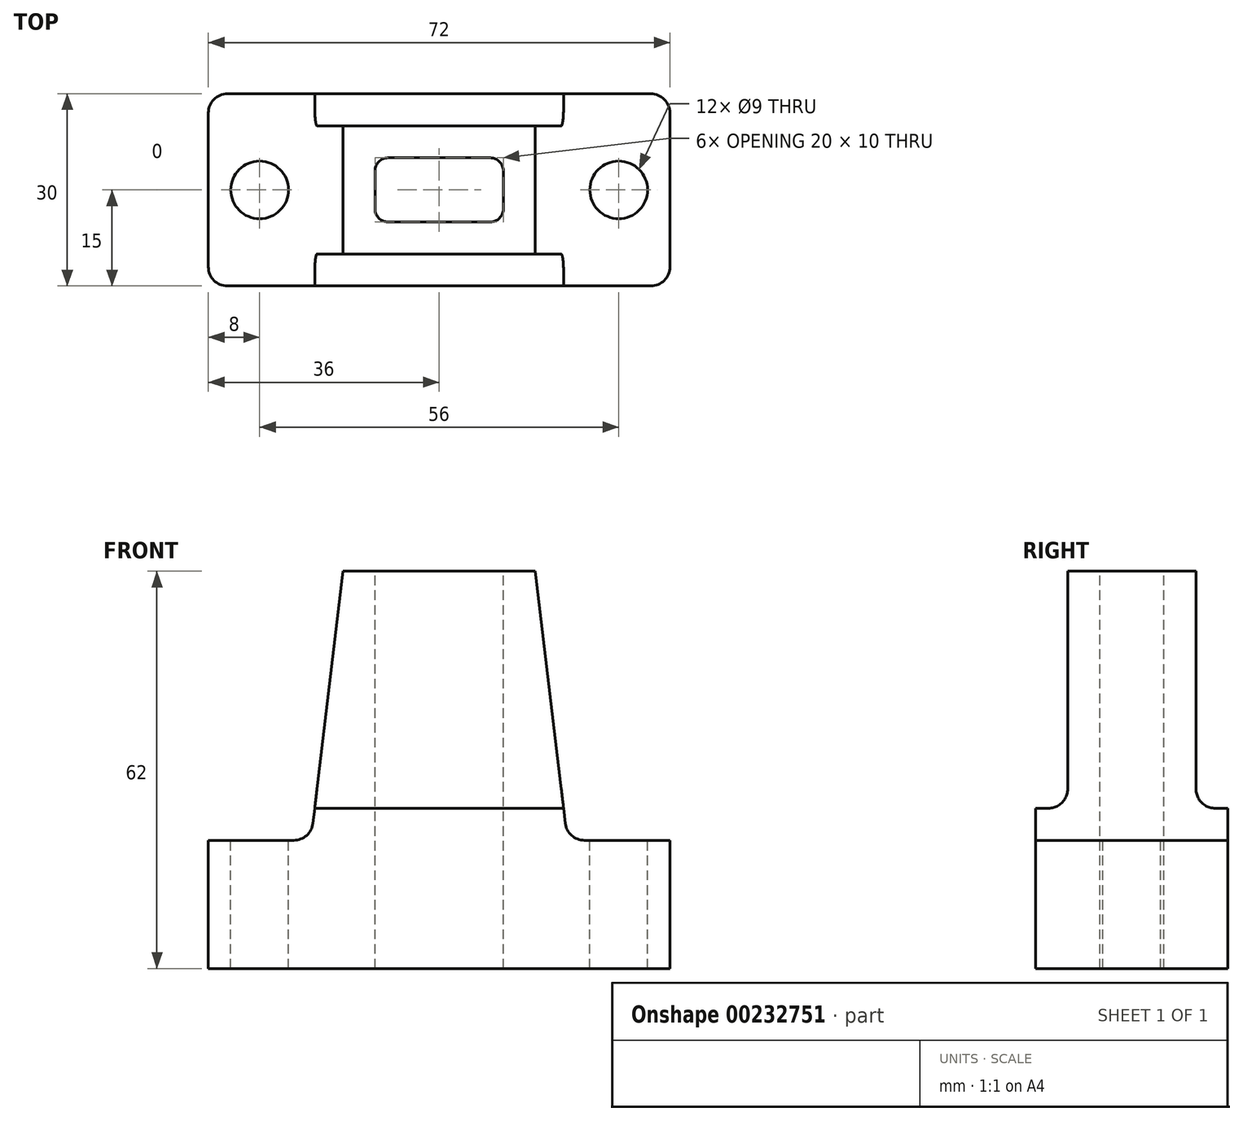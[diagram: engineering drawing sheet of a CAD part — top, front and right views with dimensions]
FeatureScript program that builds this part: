
annotation { "Feature Type Name" : "Feature", "Feature Type Description" : "" }
export const myFeature = defineFeature(function(context is Context, id is Id, definition is map)
    precondition{}
    {
        {
            var Q0;
            Q0=qCreatedBy(makeId("Top.planeOp"),FACE);
            var sketch = newSketch(context, id + "F0", { "sketchPlane" : qUnion([Q0])});
            skLineSegment(sketch, "E0.bottom", {"start": v(-36, 15) * mm, "end": v(36, 15) * mm});
            skLineSegment(sketch, "E0.top", {"start": v(-36, -15) * mm, "end": v(36, -15) * mm});
            skLineSegment(sketch, "E0.left", {"start": v(-36, 15) * mm, "end": v(-36, -15) * mm});
            skLineSegment(sketch, "E0.right", {"start": v(36, 15) * mm, "end": v(36, -15) * mm});
            skSolve(sketch);
        }
        {
            var Q0;
            Q0 = qSketchRegion(id + "F0", true);
            extrude(context, id + "F1", {"entities" : qUnion([Q0]), "depth" : 62 * mm});
        }
        {
            var Q0;
            Q0=makeQuery(id+"F1.opExtrude","SWEPT_FACE",FACE,{"disambiguationData":[OSD([sQuery(id+"F0.wireOp",EDGE,"E0.top")])]});
            var sketch = newSketch(context, id + "F2", { "sketchPlane" : qUnion([Q0])});
            skLineSegment(sketch, "E1", {"start": v(-46, 72) * mm, "end": v(-15, 72) * mm});
            skLineSegment(sketch, "E2", {"start": v(-15, 72) * mm, "end": v(-15, 62) * mm});
            skLineSegment(sketch, "E3", {"start": v(-15, 62) * mm, "end": v(-20, 20) * mm});
            skLineSegment(sketch, "E4", {"start": v(-20, 20) * mm, "end": v(-46, 20) * mm});
            skLineSegment(sketch, "E5", {"start": v(-46, 20) * mm, "end": v(-46, 72) * mm});
            skLineSegment(sketch, "E6.MirrorCS", {"start": v(15, 72) * mm, "end": v(15, 62) * mm});
            skLineSegment(sketch, "E7.MirrorCS", {"start": v(20, 20) * mm, "end": v(46, 20) * mm});
            skLineSegment(sketch, "E8.MirrorCS", {"start": v(46, 72) * mm, "end": v(15, 72) * mm});
            skLineSegment(sketch, "E9.MirrorCS", {"start": v(15, 62) * mm, "end": v(20, 20) * mm});
            skLineSegment(sketch, "E10.MirrorCS", {"start": v(46, 20) * mm, "end": v(46, 72) * mm});
            skSolve(sketch);
        }
        {
            var Q0;
            Q0 = qSketchRegion(id + "F2", true);
            extrude(context, id + "F3", {"entities" : qUnion([Q0]), "operationType" : NewBodyOperationType.REMOVE, "endBound" : BoundingType.THROUGH_ALL, "oppositeDirection" : true, "depth" : 25 * mm});
        }
        {
            var Q0;
            Q0=qCreatedBy(makeId("Right.planeOp"),FACE);
            var sketch = newSketch(context, id + "F4", { "sketchPlane" : qUnion([Q0])});
            skLineSegment(sketch, "E11.bottom", {"start": v(-25, 72) * mm, "end": v(-10, 72) * mm});
            skLineSegment(sketch, "E11.top", {"start": v(-25, 25) * mm, "end": v(-10, 25) * mm});
            skLineSegment(sketch, "E11.left", {"start": v(-25, 72) * mm, "end": v(-25, 25) * mm});
            skLineSegment(sketch, "E11.right", {"start": v(-10, 72) * mm, "end": v(-10, 25) * mm});
            skLineSegment(sketch, "E12.MirrorCS", {"start": v(10, 72) * mm, "end": v(10, 25) * mm});
            skLineSegment(sketch, "E13.MirrorCS", {"start": v(25, 72) * mm, "end": v(10, 72) * mm});
            skLineSegment(sketch, "E14.MirrorCS", {"start": v(25, 25) * mm, "end": v(10, 25) * mm});
            skLineSegment(sketch, "E15.MirrorCS", {"start": v(25, 72) * mm, "end": v(25, 25) * mm});
            skSolve(sketch);
        }
        {
            var Q0;
            Q0 = qSketchRegion(id + "F4", true);
            extrude(context, id + "F5", {"entities" : qUnion([Q0]), "operationType" : NewBodyOperationType.REMOVE, "endBound" : BoundingType.THROUGH_ALL, "oppositeDirection" : true, "depth" : 25 * mm, "hasSecondDirection" : true, "secondDirectionOppositeDirection" : false, "secondDirectionDepth" : 25 * mm});
        }
        {
            var Q0;
            Q0=makeQuery(id+"F1.opExtrude","CAP_FACE",FACE,{"disambiguationData":[OSD([sQuery(id+"F0.wireOp",EDGE,"E0.bottom"),sQuery(id+"F0.wireOp",EDGE,"E0.top"),sQuery(id+"F0.wireOp",EDGE,"E0.left"),sQuery(id+"F0.wireOp",EDGE,"E0.right")])],"isStart":false});
            var sketch = newSketch(context, id + "F6", { "sketchPlane" : qUnion([Q0])});
            skLineSegment(sketch, "E16.bottom", {"start": v(-10, 5) * mm, "end": v(10, 5) * mm});
            skLineSegment(sketch, "E16.top", {"start": v(-10, -5) * mm, "end": v(10, -5) * mm});
            skLineSegment(sketch, "E16.left", {"start": v(-10, 5) * mm, "end": v(-10, -5) * mm});
            skLineSegment(sketch, "E16.right", {"start": v(10, 5) * mm, "end": v(10, -5) * mm});
            skSolve(sketch);
        }
        {
            var Q0;
            Q0 = qSketchRegion(id + "F6", true);
            extrude(context, id + "F7", {"entities" : qUnion([Q0]), "operationType" : NewBodyOperationType.REMOVE, "endBound" : BoundingType.THROUGH_ALL, "oppositeDirection" : true, "depth" : 25 * mm});
        }
        {
            var Q0;
            Q0=makeQuery(id+"F3.boolean.opBoolean","COPY",FACE,{"derivedFrom":makeQuery(id+"F3.opExtrude","SWEPT_FACE",FACE,{"disambiguationData":[OSD([sQuery(id+"F2.wireOp",EDGE,"E7.MirrorCS")])]})});
            var sketch = newSketch(context, id + "F8", { "sketchPlane" : qUnion([Q0])});
            skPoint(sketch, "E17", {"position": v(-28, 0) * mm});
            skPoint(sketch, "E18", {"position": v(28, 0) * mm});
            skSolve(sketch);
        }
        {
            var Q0;
            Q0=sQuery(id+"F8.wireOp",VERTEX,"E17");
            var Q1;
            Q1=sQuery(id+"F8.wireOp",VERTEX,"E18");
            var Q2;
            Q2=makeQuery(id+"F1.opExtrude","SWEPT_BODY",BODY,{"disambiguationData":[OSD([sQuery(id+"F0.wireOp",EDGE,"E0.bottom"),sQuery(id+"F0.wireOp",EDGE,"E0.top"),sQuery(id+"F0.wireOp",EDGE,"E0.left"),sQuery(id+"F0.wireOp",EDGE,"E0.right")])]});
            hole(context, id + "F9", {"style" : HoleStyle.SIMPLE, "endStyle" : HoleEndStyle.THROUGH, "holeDiameter" : 9 * mm, "locations" : qUnion([Q0, Q1]), "scope" : qUnion([Q2]), "isTappedThrough" : true});
        }
        {
            var Q0;
            Q0=makeQuery(id+"F1.opExtrude","SWEPT_EDGE",EDGE,{"disambiguationData":[OSD([sQuery(id+"F0.wireOp",EDGE,"E0.bottom"),sQuery(id+"F0.wireOp",EDGE,"E0.left")])]});
            var Q1;
            Q1=makeQuery(id+"F1.opExtrude","SWEPT_EDGE",EDGE,{"disambiguationData":[OSD([sQuery(id+"F0.wireOp",EDGE,"E0.top"),sQuery(id+"F0.wireOp",EDGE,"E0.right")])]});
            var Q2;
            Q2=makeQuery(id+"F1.opExtrude","SWEPT_EDGE",EDGE,{"disambiguationData":[OSD([sQuery(id+"F0.wireOp",EDGE,"E0.bottom"),sQuery(id+"F0.wireOp",EDGE,"E0.right")])]});
            var Q3;
            Q3=makeQuery(id+"F1.opExtrude","SWEPT_EDGE",EDGE,{"disambiguationData":[OSD([sQuery(id+"F0.wireOp",EDGE,"E0.top"),sQuery(id+"F0.wireOp",EDGE,"E0.left")])]});
            fillet(context, id + "F10", {"entities" : qUnion([Q0, Q1, Q2, Q3]), "radius" : 3 * mm, "tangentPropagation" : true, "allowEdgeOverflow" : false});
        }
        {
            var Q0;
            Q0=makeQuery(id+"F3.boolean.opBoolean","COPY",EDGE,{"derivedFrom":makeQuery(id+"F3.opExtrude","SWEPT_EDGE",EDGE,{"disambiguationData":[OSD([sQuery(id+"F2.wireOp",EDGE,"E3"),sQuery(id+"F2.wireOp",EDGE,"E4")])]})});
            var Q1;
            Q1=makeQuery(id+"F3.boolean.opBoolean","COPY",EDGE,{"derivedFrom":makeQuery(id+"F3.opExtrude","SWEPT_EDGE",EDGE,{"disambiguationData":[OSD([sQuery(id+"F2.wireOp",EDGE,"E7.MirrorCS"),sQuery(id+"F2.wireOp",EDGE,"E9.MirrorCS")])]})});
            fillet(context, id + "F11", {"entities" : qUnion([Q0, Q1]), "radius" : 3 * mm, "tangentPropagation" : true, "allowEdgeOverflow" : false});
        }
        {
            var Q0;
            Q0=makeQuery(id+"F5.boolean.opBoolean","COPY",EDGE,{"derivedFrom":makeQuery(id+"F5.opExtrude","SWEPT_EDGE",EDGE,{"disambiguationData":[OSD([sQuery(id+"F4.wireOp",EDGE,"E12.MirrorCS"),sQuery(id+"F4.wireOp",EDGE,"E14.MirrorCS")])]})});
            var Q1;
            Q1=makeQuery(id+"F5.boolean.opBoolean","COPY",EDGE,{"derivedFrom":makeQuery(id+"F5.opExtrude","SWEPT_EDGE",EDGE,{"disambiguationData":[OSD([sQuery(id+"F4.wireOp",EDGE,"E11.top"),sQuery(id+"F4.wireOp",EDGE,"E11.right")])]})});
            fillet(context, id + "F12", {"entities" : qUnion([Q0, Q1]), "radius" : 3 * mm, "tangentPropagation" : true, "allowEdgeOverflow" : false});
        }
        {
            var Q0;
            Q0=makeQuery(id+"F7.boolean.opBoolean","COPY",EDGE,{"derivedFrom":makeQuery(id+"F7.opExtrude","SWEPT_EDGE",EDGE,{"disambiguationData":[OSD([sQuery(id+"F6.wireOp",EDGE,"E16.bottom"),sQuery(id+"F6.wireOp",EDGE,"E16.right")])]})});
            var Q1;
            Q1=makeQuery(id+"F7.boolean.opBoolean","COPY",EDGE,{"derivedFrom":makeQuery(id+"F7.opExtrude","SWEPT_EDGE",EDGE,{"disambiguationData":[OSD([sQuery(id+"F6.wireOp",EDGE,"E16.top"),sQuery(id+"F6.wireOp",EDGE,"E16.right")])]})});
            var Q2;
            Q2=makeQuery(id+"F7.boolean.opBoolean","COPY",EDGE,{"derivedFrom":makeQuery(id+"F7.opExtrude","SWEPT_EDGE",EDGE,{"disambiguationData":[OSD([sQuery(id+"F6.wireOp",EDGE,"E16.top"),sQuery(id+"F6.wireOp",EDGE,"E16.left")])]})});
            var Q3;
            Q3=makeQuery(id+"F7.boolean.opBoolean","COPY",EDGE,{"derivedFrom":makeQuery(id+"F7.opExtrude","SWEPT_EDGE",EDGE,{"disambiguationData":[OSD([sQuery(id+"F6.wireOp",EDGE,"E16.bottom"),sQuery(id+"F6.wireOp",EDGE,"E16.left")])]})});
            fillet(context, id + "F13", {"entities" : qUnion([Q0, Q1, Q2, Q3]), "radius" : 2 * mm, "tangentPropagation" : true, "allowEdgeOverflow" : false});
        }
    });
